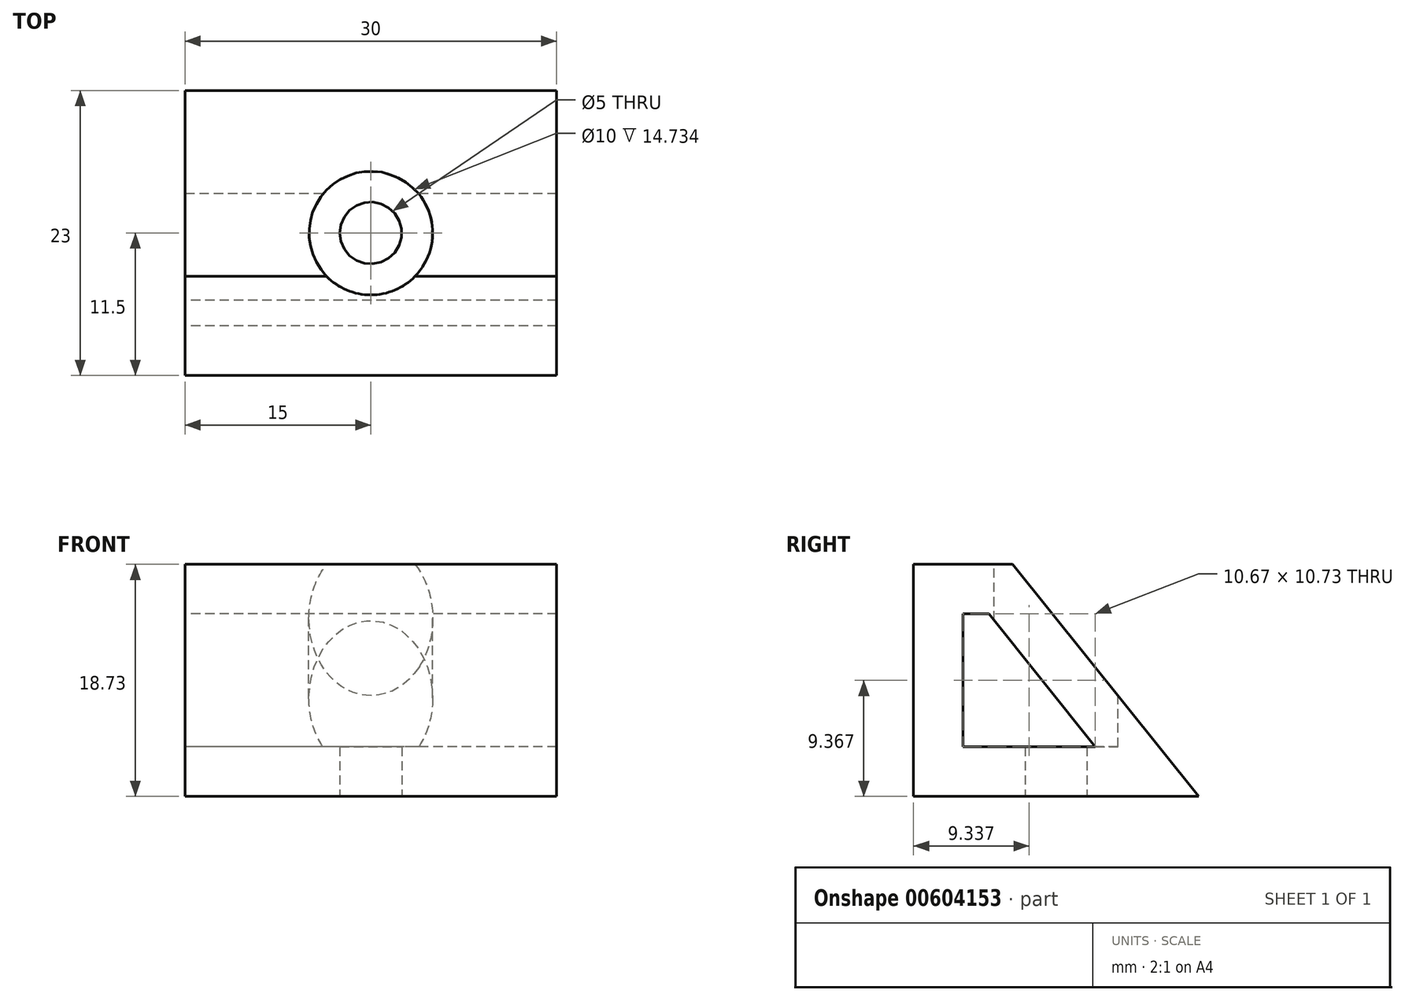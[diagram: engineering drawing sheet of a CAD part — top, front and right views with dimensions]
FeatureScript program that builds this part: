
annotation { "Feature Type Name" : "Feature", "Feature Type Description" : "" }
export const myFeature = defineFeature(function(context is Context, id is Id, definition is map)
    precondition{}
    {
        {
            var Q0;
            Q0=qCreatedBy(makeId("Right.planeOp"),FACE);
            var sketch = newSketch(context, id + "F0", { "sketchPlane" : qUnion([Q0])});
            skLineSegment(sketch, "E0", {"start": v(0, 0) * mm, "end": v(0, 18.73) * mm});
            skLineSegment(sketch, "E1", {"start": v(0, 18.73) * mm, "end": v(8, 18.73) * mm});
            skLineSegment(sketch, "E2", {"start": v(8, 18.73) * mm, "end": v(23, 0) * mm});
            skLineSegment(sketch, "E3", {"start": v(23, 0) * mm, "end": v(0, 0) * mm});
            skLineSegment(sketch, "E4.0", {"start": v(14.67, 4) * mm, "end": v(4, 4) * mm});
            skLineSegment(sketch, "E4.1", {"start": v(6.08, 14.73) * mm, "end": v(14.67, 4) * mm});
            skLineSegment(sketch, "E4.2", {"start": v(4, 14.73) * mm, "end": v(6.08, 14.73) * mm});
            skLineSegment(sketch, "E4.3", {"start": v(4, 4) * mm, "end": v(4, 14.73) * mm});
            skSolve(sketch);
        }
        {
            var Q0;
            Q0=makeQuery(id+"F0.imprint","IMPRINT",FACE,{"disambiguationData":[TD([[makeQuery(id+"F0.imprint","IMPRINT",EDGE,{"derivedFrom":sQuery(id+"F0.wireOp",EDGE,"E0")}),-1.0]])]});
            extrude(context, id + "F1", {"entities" : qUnion([Q0]), "depth" : 30 * mm, "offsetDistance" : 25 * mm});
        }
        {
            var Q0;
            Q0=makeQuery(id+"F1.opExtrude","SWEPT_FACE",FACE,{"disambiguationData":[OSD([sQuery(id+"F0.wireOp",EDGE,"E3")])]});
            var sketch = newSketch(context, id + "F2", { "sketchPlane" : qUnion([Q0])});
            skLineSegment(sketch, "E5", {"start": v(30, -11.5) * mm, "end": v(0, -11.5) * mm, "construction": true});
            skCircle(sketch, "E6", {"center": v(15, -11.5) * mm, "radius": 2.5 * mm});
            skSolve(sketch);
        }
        {
            var Q0;
            Q0 = qSketchRegion(id + "F2", true);
            extrude(context, id + "F3", {"entities" : qUnion([Q0]), "operationType" : NewBodyOperationType.REMOVE, "oppositeDirection" : true, "depth" : 4 * mm, "offsetDistance" : 25 * mm});
        }
        {
            var Q0;
            Q0=makeQuery(id+"F1.opExtrude","SWEPT_FACE",FACE,{"disambiguationData":[OSD([sQuery(id+"F0.wireOp",EDGE,"E1")])]});
            var sketch = newSketch(context, id + "F4", { "sketchPlane" : qUnion([Q0])});
            skLineSegment(sketch, "E7", {"start": v(15, 0) * mm, "end": v(15, 11.5) * mm, "construction": true});
            skCircle(sketch, "E8", {"center": v(15, 11.5) * mm, "radius": 5 * mm});
            skSolve(sketch);
        }
        {
            var Q0;
            Q0 = qSketchRegion(id + "F4", true);
            extrude(context, id + "F5", {"entities" : qUnion([Q0]), "operationType" : NewBodyOperationType.REMOVE, "oppositeDirection" : true, "depth" : 14.73 * mm, "offsetDistance" : 25 * mm});
        }
    });
